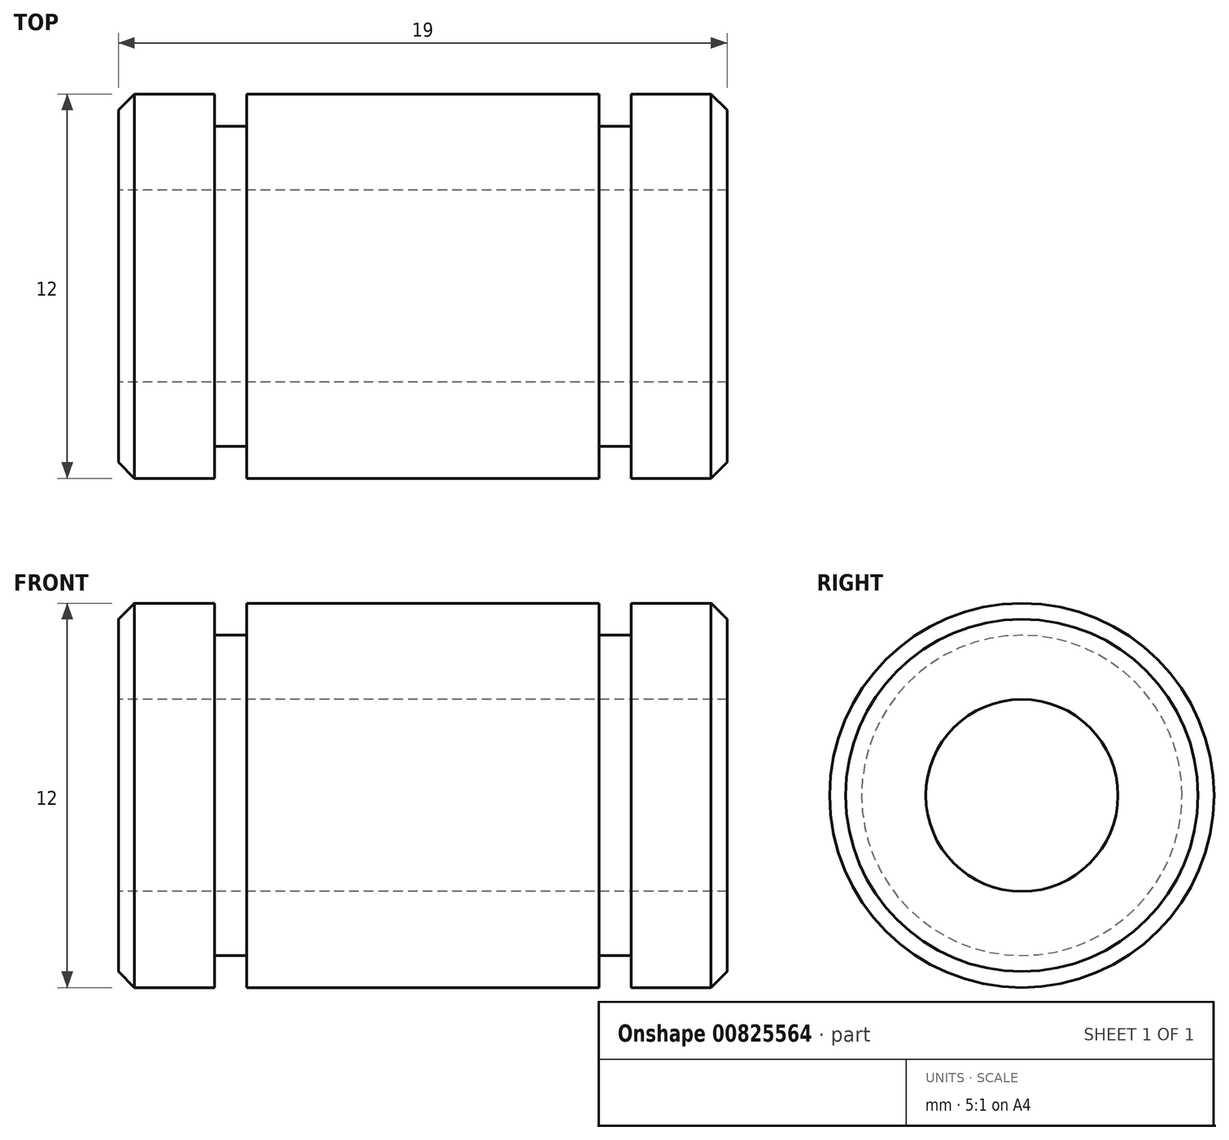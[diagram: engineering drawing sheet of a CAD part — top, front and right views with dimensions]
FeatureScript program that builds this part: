
annotation { "Feature Type Name" : "Feature", "Feature Type Description" : "" }
export const myFeature = defineFeature(function(context is Context, id is Id, definition is map)
    precondition{}
    {
        {
            var Q0;
            Q0=qCreatedBy(makeId("Front.planeOp"),FACE);
            var sketch = newSketch(context, id + "F0", { "sketchPlane" : qUnion([Q0])});
            skLineSegment(sketch, "E0", {"start": v(-9.5, 3) * mm, "end": v(9.5, 3) * mm});
            skPoint(sketch, "E1", {"position": v(0, 3) * mm});
            skLineSegment(sketch, "E2", {"start": v(-9.5, 3) * mm, "end": v(-9.5, 6) * mm});
            skLineSegment(sketch, "E3", {"start": v(-9.5, 6) * mm, "end": v(-6.5, 6) * mm});
            skLineSegment(sketch, "E4", {"start": v(-6.5, 6) * mm, "end": v(-6.5, 5) * mm});
            skLineSegment(sketch, "E5", {"start": v(-6.5, 5) * mm, "end": v(-5.5, 5) * mm});
            skLineSegment(sketch, "E6", {"start": v(-5.5, 5) * mm, "end": v(-5.5, 6) * mm});
            skLineSegment(sketch, "E7", {"start": v(-5.5, 6) * mm, "end": v(0, 6) * mm});
            skLineSegment(sketch, "E8.MirrorCS", {"start": v(5.5, 5) * mm, "end": v(5.5, 6) * mm});
            skLineSegment(sketch, "E9.MirrorCS", {"start": v(6.5, 5) * mm, "end": v(5.5, 5) * mm});
            skLineSegment(sketch, "E10.MirrorCS", {"start": v(6.5, 6) * mm, "end": v(6.5, 5) * mm});
            skLineSegment(sketch, "E11.MirrorCS", {"start": v(9.5, 6) * mm, "end": v(6.5, 6) * mm});
            skLineSegment(sketch, "E12.MirrorCS", {"start": v(9.5, 3) * mm, "end": v(9.5, 6) * mm});
            skLineSegment(sketch, "E13.MirrorCS", {"start": v(5.5, 6) * mm, "end": v(0, 6) * mm});
            skLineSegment(sketch, "E14", {"start": v(0, 0) * mm, "end": v(13.33, 0) * mm, "construction": true});
            skSolve(sketch);
        }
        {
            var Q0;
            Q0 = qSketchRegion(id + "F0", true);
            var Q1;
            Q1=sQuery(id+"F0.wireOp",EDGE,"E14");
            revolve(context, id + "F1", {"surfaceOperationType" : NewSurfaceOperationType.NEW, "entities" : qUnion([Q0]), "axis" : qUnion([Q1]), "revolveType" : RevolveType.FULL});
        }
        {
            var Q0;
            Q0=makeQuery(id+"F1.opRevolve","SWEPT_EDGE",EDGE,{"disambiguationData":[OSD([sQuery(id+"F0.wireOp",EDGE,"E2"),sQuery(id+"F0.wireOp",EDGE,"E3")])]});
            var Q1;
            Q1=makeQuery(id+"F1.opRevolve","SWEPT_EDGE",EDGE,{"disambiguationData":[OSD([sQuery(id+"F0.wireOp",EDGE,"E11.MirrorCS"),sQuery(id+"F0.wireOp",EDGE,"E12.MirrorCS")])]});
            chamfer(context, id + "F2", {"entities" : qUnion([Q0, Q1]), "width" : 0.5 * mm, "tangentPropagation" : true});
        }
    });
